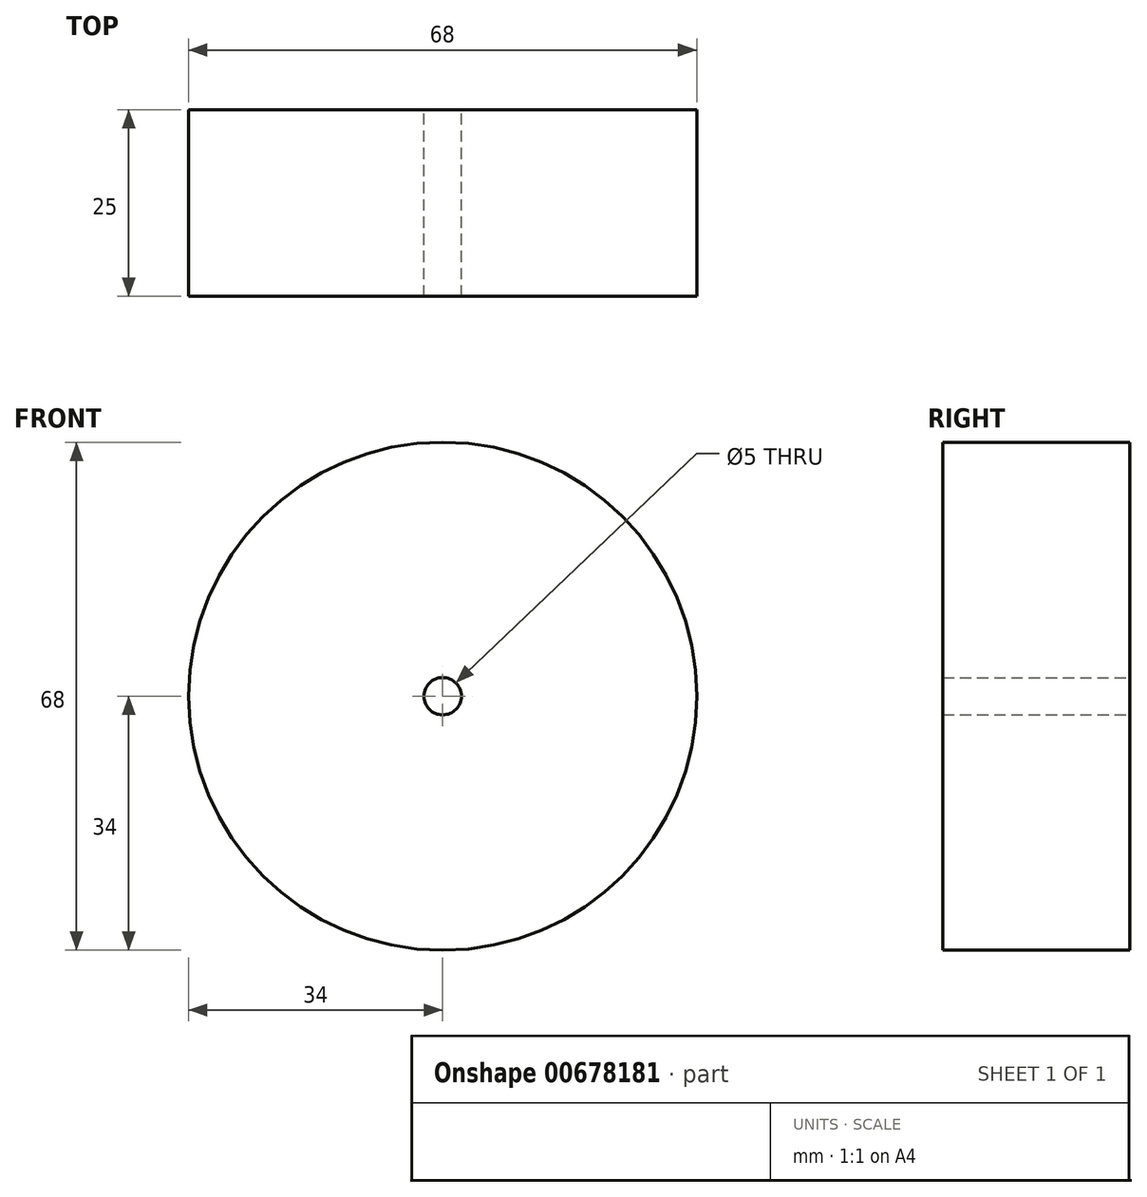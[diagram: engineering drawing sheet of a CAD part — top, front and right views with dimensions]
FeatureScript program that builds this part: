
annotation { "Feature Type Name" : "Feature", "Feature Type Description" : "" }
export const myFeature = defineFeature(function(context is Context, id is Id, definition is map)
    precondition{}
    {
        {
            var Q0;
            Q0=qCreatedBy(makeId("Front.planeOp"),FACE);
            var sketch = newSketch(context, id + "F0", { "sketchPlane" : qUnion([Q0])});
            skCircle(sketch, "E0", {"center": v(0, 0) * mm, "radius": 34 * mm});
            skCircle(sketch, "E1", {"center": v(0, 0) * mm, "radius": 2.5 * mm});
            skSolve(sketch);
        }
        {
            var Q0;
            Q0=qSketchRegion(id+"F0",true);
            extrude(context, id + "F1", {"entities" : qUnion([Q0]), "depth" : 25 * mm, "offsetDistance" : 25 * mm});
        }
    });
